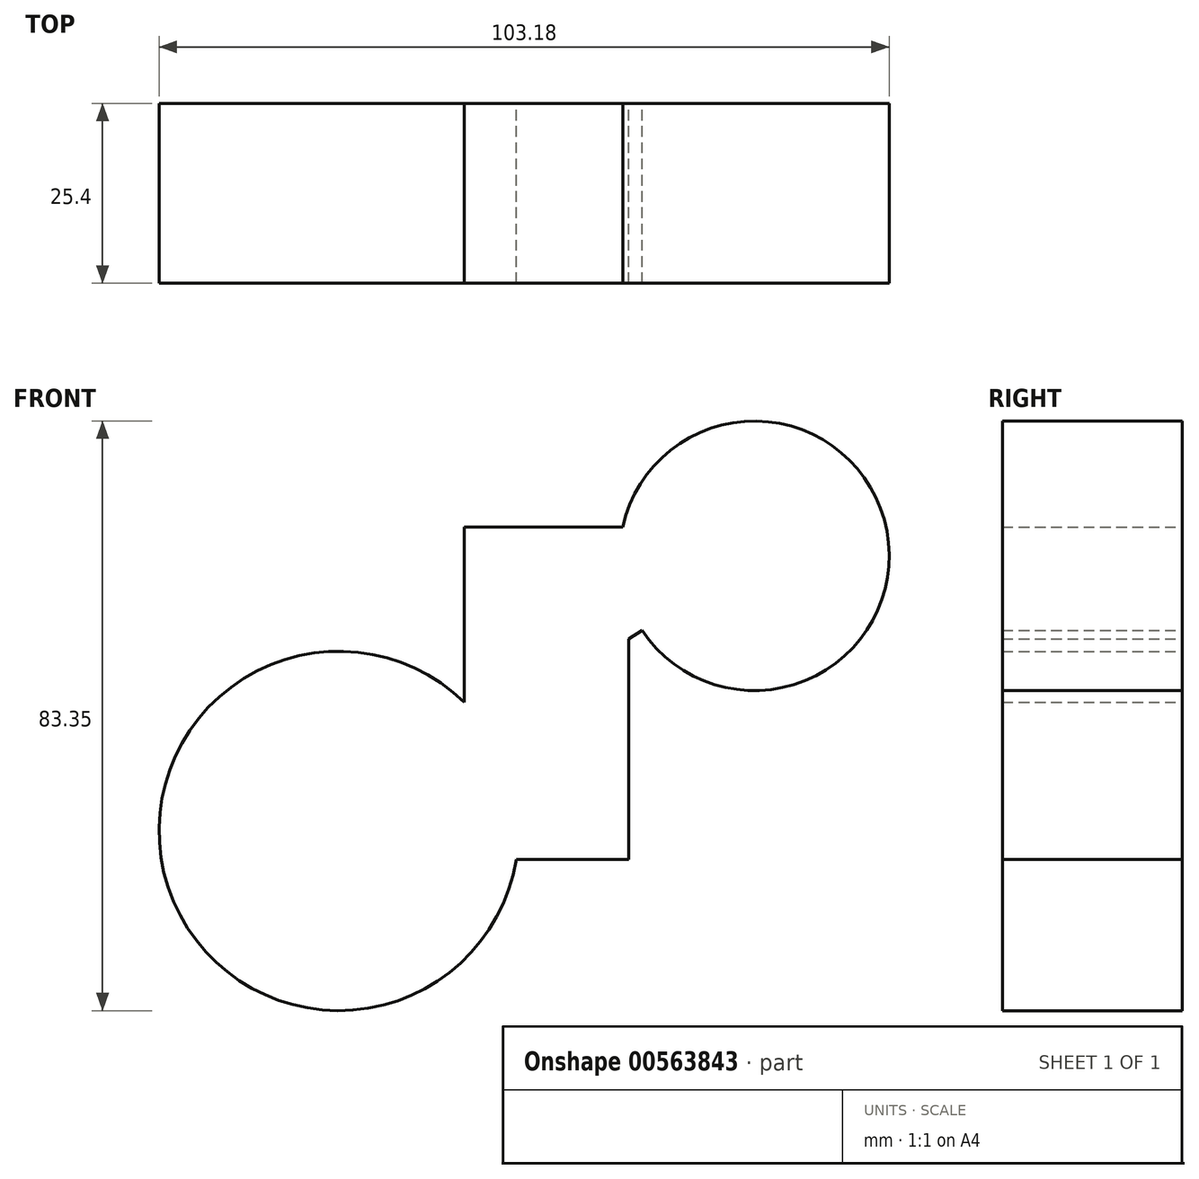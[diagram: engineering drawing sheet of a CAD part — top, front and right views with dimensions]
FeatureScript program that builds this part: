
annotation { "Feature Type Name" : "Feature", "Feature Type Description" : "" }
export const myFeature = defineFeature(function(context is Context, id is Id, definition is map)
    precondition{}
    {
        {
            var Q0;
            Q0=qCreatedBy(makeId("Front.planeOp"),FACE);
            var sketch = newSketch(context, id + "F0", { "sketchPlane" : qUnion([Q0])});
            skCircle(sketch, "E0", {"center": v(17.75, 42.95) * mm, "radius": 19.05 * mm});
            skCircle(sketch, "E1", {"center": v(-40.98, 4.05) * mm, "radius": 25.4 * mm});
            skLineSegment(sketch, "E2", {"start": v(-40.98, 4.05) * mm, "end": v(17.75, 42.95) * mm});
            skLineSegment(sketch, "E3.bottom", {"start": v(0, 0) * mm, "end": v(-23.23, 0) * mm});
            skLineSegment(sketch, "E3.top", {"start": v(0, 47) * mm, "end": v(-23.23, 47) * mm});
            skLineSegment(sketch, "E3.left", {"start": v(0, 0) * mm, "end": v(0, 47) * mm});
            skLineSegment(sketch, "E3.right", {"start": v(-23.23, 0) * mm, "end": v(-23.23, 47) * mm});
            skPoint(sketch, "E3.middle", {"position": v(-11.62, 23.5) * mm});
            skSolve(sketch);
        }
        {
            var Q0;
            Q0 = qSketchRegion(id + "F0", true);
            extrude(context, id + "F1", {"entities" : qUnion([Q0]), "depth" : 25.4 * mm, "offsetDistance" : 25.4 * mm});
        }
    });
